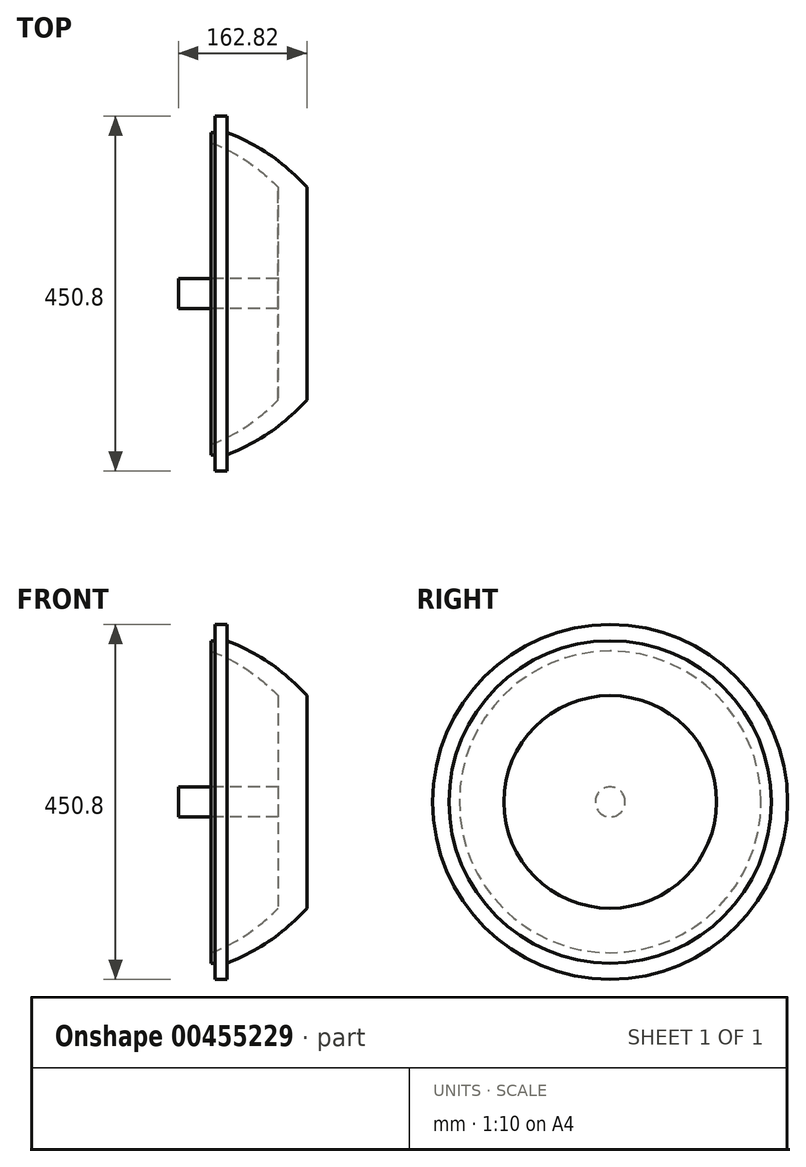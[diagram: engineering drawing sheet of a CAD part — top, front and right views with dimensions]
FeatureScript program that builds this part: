
annotation { "Feature Type Name" : "Feature", "Feature Type Description" : "" }
export const myFeature = defineFeature(function(context is Context, id is Id, definition is map)
    precondition{}
    {
        {
            var Q0;
            Q0=qCreatedBy(makeId("Front.planeOp"),FACE);
            var sketch = newSketch(context, id + "F0", { "sketchPlane" : qUnion([Q0])});
            skLineSegment(sketch, "E0", {"start": v(-67.43, -36.7) * mm, "end": v(-29.05, -36.7) * mm});
            skLineSegment(sketch, "E1", {"start": v(-67.43, -36.7) * mm, "end": v(-67.43, -36.7) * mm});
            skLineSegment(sketch, "E2", {"start": v(97.15, -17.7) * mm, "end": v(-29.05, -17.7) * mm});
            skLineSegment(sketch, "E3", {"start": v(-29.05, -17.7) * mm, "end": v(-29.05, -36.7) * mm});
            skLineSegment(sketch, "E4", {"start": v(-93.58, -36.7) * mm, "end": v(72.06, -36.7) * mm, "construction": true});
            skLineSegment(sketch, "E5", {"start": v(-67.43, -36.7) * mm, "end": v(97.15, -36.7) * mm});
            skPoint(sketch, "E6.start.orphan", {"position": v(-67.43, -36.7) * mm});
            skLineSegment(sketch, "E7", {"start": v(97.15, -36.7) * mm, "end": v(97.15, -17.7) * mm});
            skLineSegment(sketch, "E8", {"start": v(97.15, -17.7) * mm, "end": v(97.15, 98.4) * mm});
            skLineSegment(sketch, "E9", {"start": v(11.95, 154.92) * mm, "end": v(11.95, 168.09) * mm});
            skLineSegment(sketch, "E10", {"start": v(11.95, 168.09) * mm, "end": v(17.45, 168.09) * mm});
            skLineSegment(sketch, "E11", {"start": v(17.45, 168.09) * mm, "end": v(17.45, 188.7) * mm});
            skLineSegment(sketch, "E12", {"start": v(17.45, 188.7) * mm, "end": v(32.45, 188.7) * mm});
            skLineSegment(sketch, "E13", {"start": v(32.45, 188.7) * mm, "end": v(32.45, 168.09) * mm});
            skArc(sketch, "E14", {"start": v(97.15, 98.4) * mm, "mid": v(57.75, 131.49) * mm, "end": v(11.95, 154.92) * mm});
            skArc(sketch, "E15", {"start": v(133.77, 98.4) * mm, "mid": v(87.21, 139.22) * mm, "end": v(32.45, 168.09) * mm});
            skLineSegment(sketch, "E16", {"start": v(97.15, -36.7) * mm, "end": v(133.77, -36.7) * mm});
            skLineSegment(sketch, "E17", {"start": v(133.77, -36.7) * mm, "end": v(133.77, 98.4) * mm});
            skLineSegment(sketch, "E18", {"start": v(-29.05, -17.7) * mm, "end": v(-29.05, 199.68) * mm, "construction": true});
            skLineSegment(sketch, "E19", {"start": v(-29.05, 199.68) * mm, "end": v(-29.05, 178.4) * mm, "construction": true});
            skPoint(sketch, "E19.endSnap0", {"position": v(17.45, 178.4) * mm});
            skLineSegment(sketch, "E20", {"start": v(-29.05, 178.4) * mm, "end": v(17.45, 178.4) * mm, "construction": true});
            skSolve(sketch);
        }
        {
            var Q0;
            Q0=makeQuery(id+"F0.imprint","IMPRINT",FACE,{"disambiguationData":[TD([[makeQuery(id+"F0.imprint","IMPRINT",EDGE,{"derivedFrom":sQuery(id+"F0.wireOp",EDGE,"E0")}),1.0]])]});
            var Q1;
            Q1=makeQuery(id+"F0.imprint","IMPRINT",FACE,{"disambiguationData":[TD([[makeQuery(id+"F0.imprint","IMPRINT",EDGE,{"derivedFrom":sQuery(id+"F0.wireOp",EDGE,"E7")}),-1.0]])]});
            var Q2;
            Q2=makeQuery(id+"F0.imprint","IMPRINT",FACE,{"disambiguationData":[TD([[makeQuery(id+"F0.imprint","IMPRINT",EDGE,{"derivedFrom":sQuery(id+"F0.wireOp",EDGE,"E2")}),1.0]])]});
            var Q3;
            Q3=sQuery(id+"F0.wireOp",EDGE,"E4");
            revolve(context, id + "F1", {"surfaceOperationType" : NewSurfaceOperationType.NEW, "entities" : qUnion([Q0, Q1, Q2]), "axis" : qUnion([Q3]), "revolveType" : RevolveType.FULL});
        }
    });
